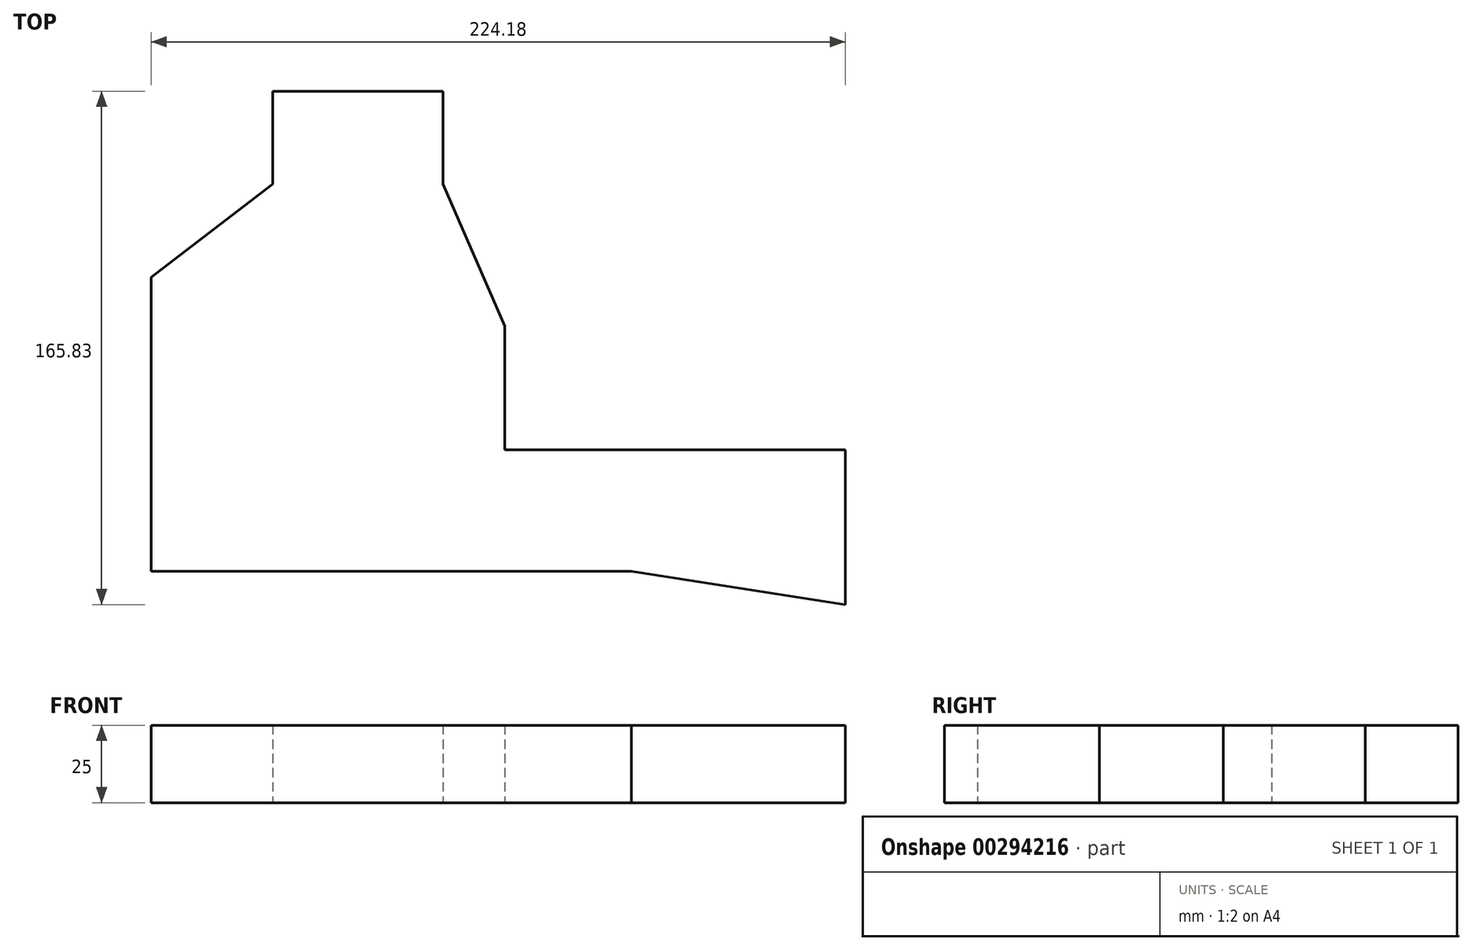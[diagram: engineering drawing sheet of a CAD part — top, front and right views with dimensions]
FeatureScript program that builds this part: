
annotation { "Feature Type Name" : "Feature", "Feature Type Description" : "" }
export const myFeature = defineFeature(function(context is Context, id is Id, definition is map)
    precondition{}
    {
        {
            var Q0;
            Q0=qCreatedBy(makeId("Top.planeOp"),FACE);
            var sketch = newSketch(context, id + "F0", { "sketchPlane" : qUnion([Q0])});
            skPoint(sketch, "E0.start.orphan", {"position": v(-75.04, 0) * mm});
            skLineSegment(sketch, "E1", {"start": v(0, 0) * mm, "end": v(0, 50) * mm});
            skLineSegment(sketch, "E2", {"start": v(0, 50) * mm, "end": v(-110, 50) * mm});
            skLineSegment(sketch, "E3", {"start": v(-110, 50) * mm, "end": v(-110, 90) * mm});
            skLineSegment(sketch, "E4", {"start": v(-130, 165.83) * mm, "end": v(-185, 165.83) * mm});
            skLineSegment(sketch, "E5", {"start": v(-130, 165.83) * mm, "end": v(-130, 135.83) * mm});
            skLineSegment(sketch, "E6", {"start": v(-130, 135.83) * mm, "end": v(-110, 90) * mm});
            skLineSegment(sketch, "E7", {"start": v(-185, 165.83) * mm, "end": v(-185, 135.83) * mm});
            skLineSegment(sketch, "E8", {"start": v(-224.18, 105.7) * mm, "end": v(-224.18, 10.7) * mm});
            skLineSegment(sketch, "E9", {"start": v(-185, 135.83) * mm, "end": v(-224.18, 105.7) * mm});
            skLineSegment(sketch, "E10", {"start": v(-224.18, 10.7) * mm, "end": v(-69.18, 10.7) * mm});
            skLineSegment(sketch, "E11", {"start": v(-69.18, 10.7) * mm, "end": v(0, 0) * mm});
            skSolve(sketch);
        }
        {
            var Q0;
            Q0=makeQuery(id+"F0.imprint","IMPRINT",FACE,{"disambiguationData":[TD([[makeQuery(id+"F0.imprint","IMPRINT",EDGE,{"derivedFrom":sQuery(id+"F0.wireOp",EDGE,"E1")}),1.0]])]});
            extrude(context, id + "F1", {"entities" : qUnion([Q0]), "depth" : 25 * mm});
        }
    });
